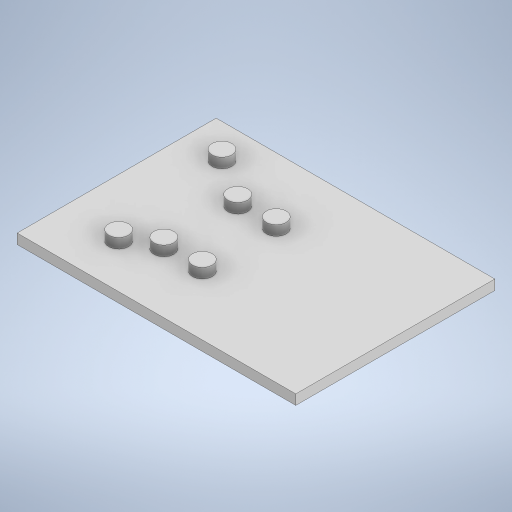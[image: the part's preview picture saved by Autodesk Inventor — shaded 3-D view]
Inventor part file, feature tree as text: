
AUTODESK INVENTOR PART (.ipt)
format: ipt  version: 2024 (Build 280153000, 153)  size: 241,664 bytes
history: native  units: mm
features: extrude x2, sketch x2
ambient origin geometry x8: Origin, YZ Plane, XZ Plane, XY Plane, X Axis, Y Axis, Z Axis, Center Point
bodies: Solid1 (feature_tree)
feature tree (4):
  extrude  "Extrusion1"  Depth=100.0mm
  extrude  "Extrusion2"  Depth=10.0mm
  sketch  "Sketch1"  dims[d0=140.0mm d1=100.0mm]
  sketch  "Sketch2"  dims[d2=5.0mm d3=0.0mm d4=10.0mm d5=10.0mm d6=10.0mm d7=10.0mm d8=10.0mm d9=10.0mm d10=5.0mm d11=0.0mm]
